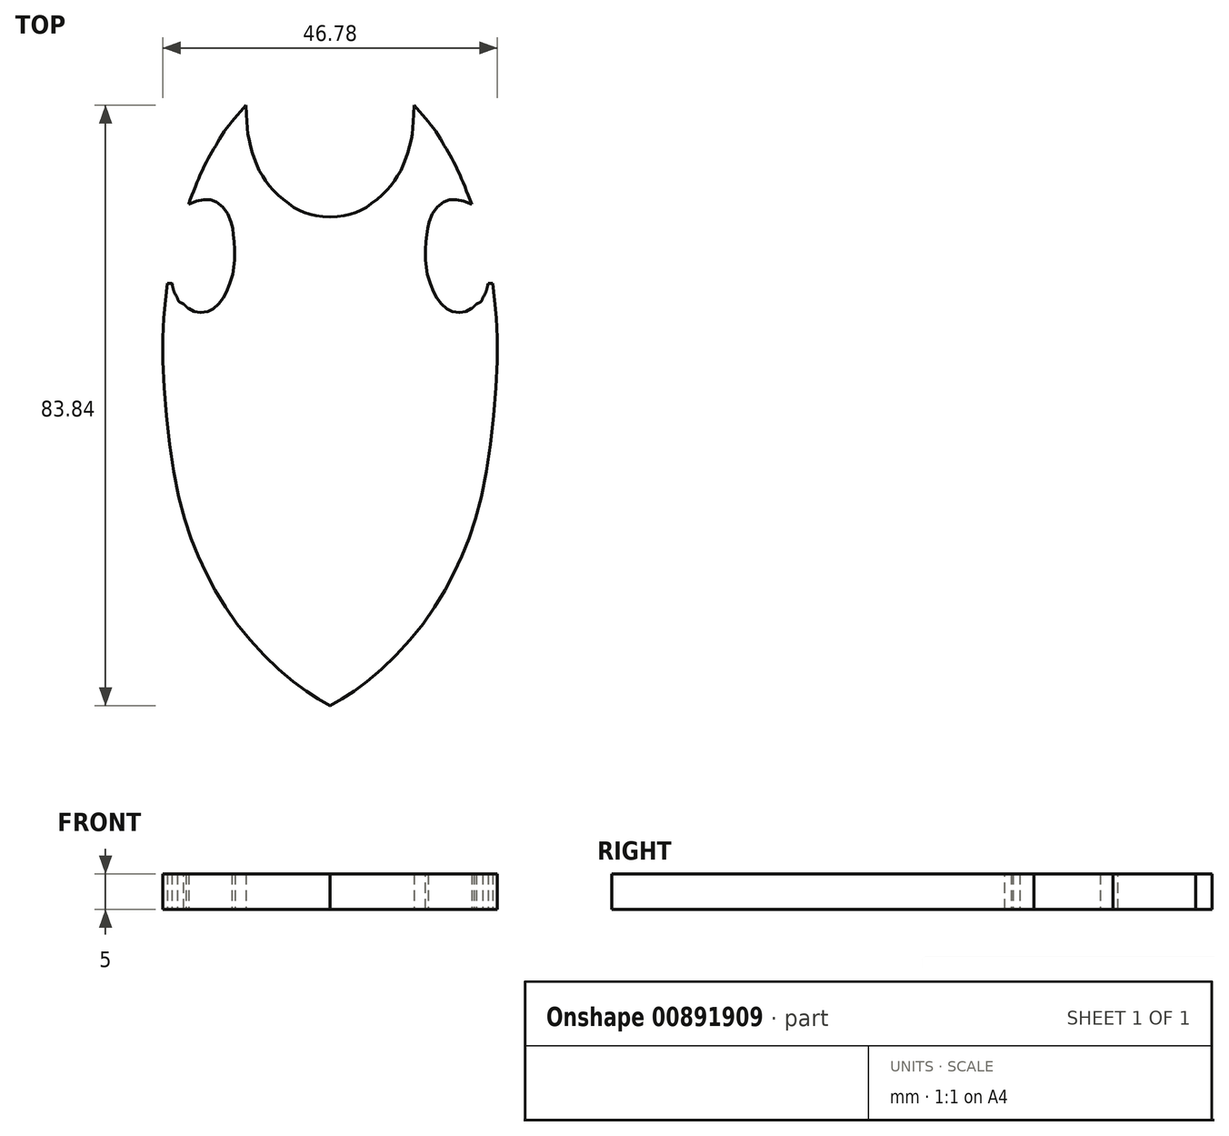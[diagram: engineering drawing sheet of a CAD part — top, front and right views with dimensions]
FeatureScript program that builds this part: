
annotation { "Feature Type Name" : "Feature", "Feature Type Description" : "" }
export const myFeature = defineFeature(function(context is Context, id is Id, definition is map)
    precondition{}
    {
        {
            var Q0;
            Q0=qCreatedBy(makeId("Top.planeOp"),FACE);
            var sketch = newSketch(context, id + "F0", { "sketchPlane" : qUnion([Q0])});
            skLineSegment(sketch, "E0", {"start": v(-34.83, -16.42) * mm, "end": v(-34.83, 59.89) * mm});
            skFitSpline(sketch, "E1", {"points": [v(-46.56, 67.52) * mm, v(-48.56, 65.23) * mm], "startDerivative": vector(-2, -2.29) * mm, "endDerivative": vector(-2, -2.29) * mm});
            skFitSpline(sketch, "E2", {"points": [v(-34.83, 51.91) * mm, v(-35.97, 51.96) * mm, v(-37.03, 52.13) * mm, v(-37.77, 52.34) * mm, v(-38.53, 52.6) * mm, v(-39.12, 52.88) * mm, v(-39.91, 53.27) * mm, v(-40.62, 53.77) * mm, v(-41.44, 54.39) * mm, v(-42.08, 54.96) * mm, v(-42.88, 55.73) * mm, v(-43.44, 56.41) * mm, v(-43.91, 57.07) * mm, v(-44.22, 57.56) * mm, v(-44.68, 58.32) * mm, v(-45.46, 60.21) * mm, v(-45.9, 61.53) * mm, v(-46.13, 62.6) * mm, v(-46.27, 63.21) * mm, v(-46.37, 64) * mm, v(-46.45, 64.87) * mm, v(-46.5, 65.8) * mm, v(-46.56, 67.52) * mm], "startDerivative": vector(-23.02, 0.41) * mm, "endDerivative": vector(-0.76, 30.45) * mm});
            skFitSpline(sketch, "E3", {"points": [v(-48.56, 65.23) * mm, v(-49.75, 63.65) * mm, v(-50.7, 62.05) * mm, v(-51.53, 60.69) * mm, v(-52.31, 59.23) * mm, v(-52.91, 57.93) * mm, v(-53.7, 56.06) * mm, v(-54.61, 53.68) * mm], "startDerivative": vector(-8.39, -10.5) * mm, "endDerivative": vector(-5.51, -14.52) * mm});
            skFitSpline(sketch, "E4", {"points": [v(-54.61, 53.68) * mm, v(-53.33, 54.2) * mm, v(-52.23, 54.36) * mm, v(-51.37, 54.32) * mm, v(-50.57, 53.94) * mm, v(-49.6, 53.08) * mm, v(-48.87, 51.76) * mm, v(-48.5, 50.62) * mm, v(-48.4, 49.88) * mm, v(-48.3, 48.98) * mm, v(-48.2, 48.01) * mm, v(-48.15, 46.21) * mm, v(-48.3, 44.89) * mm, v(-48.43, 43.93) * mm, v(-49.07, 42.09) * mm, v(-49.45, 41.03) * mm, v(-50, 40.23) * mm, v(-50.8, 39.37) * mm, v(-51.54, 38.86) * mm, v(-52.16, 38.63) * mm, v(-53.38, 38.6) * mm, v(-54.01, 38.8) * mm, v(-54.76, 39.25) * mm, v(-55.37, 39.8) * mm, v(-56.12, 40.44) * mm, v(-56.52, 42.63) * mm], "startDerivative": vector(31.12, 14.65) * mm, "endDerivative": vector(-31.39, -5.43) * mm});
            skFitSpline(sketch, "E5", {"points": [v(-54.6, 39.13) * mm, v(-55.22, 39.68) * mm, v(-56.4, 41.03) * mm, v(-56.92, 42.64) * mm], "startDerivative": vector(-2.13, 1.88) * mm, "endDerivative": vector(-0.87, 4.5) * mm});
            skFitSpline(sketch, "E6", {"points": [v(-56.92, 42.64) * mm, v(-57.56, 42.64) * mm], "startDerivative": vector(-0.64, 0) * mm, "endDerivative": vector(-0.64, 0) * mm});
            skFitSpline(sketch, "E7", {"points": [v(-57.56, 42.64) * mm, v(-58.22, 33.07) * mm, v(-56.12, 13.53) * mm, v(-52.47, 2.86) * mm, v(-47.05, -5.93) * mm, v(-39.55, -13.31) * mm, v(-34.83, -16.32) * mm], "startDerivative": vector(-6.6, -53.54) * mm, "endDerivative": vector(37.28, -21.05) * mm});
            skFitSpline(sketch, "E8.MirrorCS", {"points": [v(-23.1, 67.52) * mm, v(-21.1, 65.23) * mm], "startDerivative": vector(2, -2.29) * mm, "endDerivative": vector(2, -2.29) * mm});
            skFitSpline(sketch, "E9.MirrorCS", {"points": [v(-12.75, 42.64) * mm, v(-12.1, 42.64) * mm], "startDerivative": vector(0.64, 0) * mm, "endDerivative": vector(0.64, 0) * mm});
            skFitSpline(sketch, "E10.MirrorCS", {"points": [v(-15.06, 39.13) * mm, v(-14.45, 39.68) * mm, v(-13.26, 41.03) * mm, v(-12.75, 42.64) * mm], "startDerivative": vector(2.13, 1.88) * mm, "endDerivative": vector(0.87, 4.5) * mm});
            skFitSpline(sketch, "E11.MirrorCS", {"points": [v(-34.83, 51.91) * mm, v(-33.7, 51.96) * mm, v(-32.63, 52.13) * mm, v(-31.9, 52.34) * mm, v(-31.13, 52.6) * mm, v(-30.55, 52.88) * mm, v(-29.75, 53.27) * mm, v(-29.05, 53.77) * mm, v(-28.23, 54.39) * mm, v(-27.59, 54.96) * mm, v(-26.79, 55.73) * mm, v(-26.23, 56.41) * mm, v(-25.75, 57.07) * mm, v(-25.44, 57.56) * mm, v(-24.99, 58.32) * mm, v(-24.2, 60.21) * mm, v(-23.78, 61.53) * mm, v(-23.54, 62.6) * mm, v(-23.4, 63.21) * mm, v(-23.3, 64) * mm, v(-23.22, 64.87) * mm, v(-23.16, 65.8) * mm, v(-23.1, 67.52) * mm], "startDerivative": vector(23.02, 0.41) * mm, "endDerivative": vector(0.76, 30.45) * mm});
            skFitSpline(sketch, "E12.MirrorCS", {"points": [v(-21.1, 65.23) * mm, v(-19.92, 63.65) * mm, v(-18.96, 62.05) * mm, v(-18.14, 60.69) * mm, v(-17.35, 59.23) * mm, v(-16.75, 57.93) * mm, v(-15.97, 56.06) * mm, v(-15.06, 53.68) * mm], "startDerivative": vector(8.39, -10.5) * mm, "endDerivative": vector(5.51, -14.52) * mm});
            skFitSpline(sketch, "E13.MirrorCS", {"points": [v(-15.06, 53.68) * mm, v(-16.33, 54.2) * mm, v(-17.44, 54.36) * mm, v(-18.3, 54.32) * mm, v(-19.1, 53.94) * mm, v(-20.06, 53.08) * mm, v(-20.8, 51.76) * mm, v(-21.16, 50.62) * mm, v(-21.26, 49.88) * mm, v(-21.36, 48.98) * mm, v(-21.46, 48.01) * mm, v(-21.52, 46.21) * mm, v(-21.36, 44.89) * mm, v(-21.24, 43.93) * mm, v(-20.6, 42.09) * mm, v(-20.22, 41.03) * mm, v(-19.66, 40.23) * mm, v(-18.86, 39.37) * mm, v(-18.12, 38.86) * mm, v(-17.5, 38.63) * mm, v(-16.29, 38.6) * mm, v(-15.65, 38.8) * mm, v(-14.9, 39.25) * mm, v(-14.3, 39.8) * mm, v(-13.55, 40.44) * mm, v(-13.14, 42.63) * mm], "startDerivative": vector(-31.12, 14.65) * mm, "endDerivative": vector(31.39, -5.43) * mm});
            skFitSpline(sketch, "E14.MirrorCS", {"points": [v(-12.1, 42.64) * mm, v(-11.44, 33.07) * mm, v(-13.55, 13.53) * mm, v(-17.2, 2.86) * mm, v(-22.62, -5.93) * mm, v(-30.12, -13.31) * mm, v(-34.83, -16.32) * mm], "startDerivative": vector(6.6, -53.54) * mm, "endDerivative": vector(-37.28, -21.05) * mm});
            skSolve(sketch);
        }
        {
            var Q0;
            Q0=makeQuery(id+"F0.imprint","IMPRINT",FACE,{"disambiguationData":[TD([[makeQuery(id+"F0.imprint","IMPRINT",EDGE,{"derivedFrom":sQuery(id+"F0.wireOp",EDGE,"E1")}),1.0]])]});
            var Q1;
            Q1=makeQuery(id+"F0.imprint","IMPRINT",FACE,{"disambiguationData":[TD([[makeQuery(id+"F0.imprint","IMPRINT",EDGE,{"derivedFrom":sQuery(id+"F0.wireOp",EDGE,"E8.MirrorCS")}),-1.0]])]});
            extrude(context, id + "F1", {"entities" : qUnion([Q0, Q1]), "depth" : 5 * mm, "offsetDistance" : 25 * mm});
        }
    });
